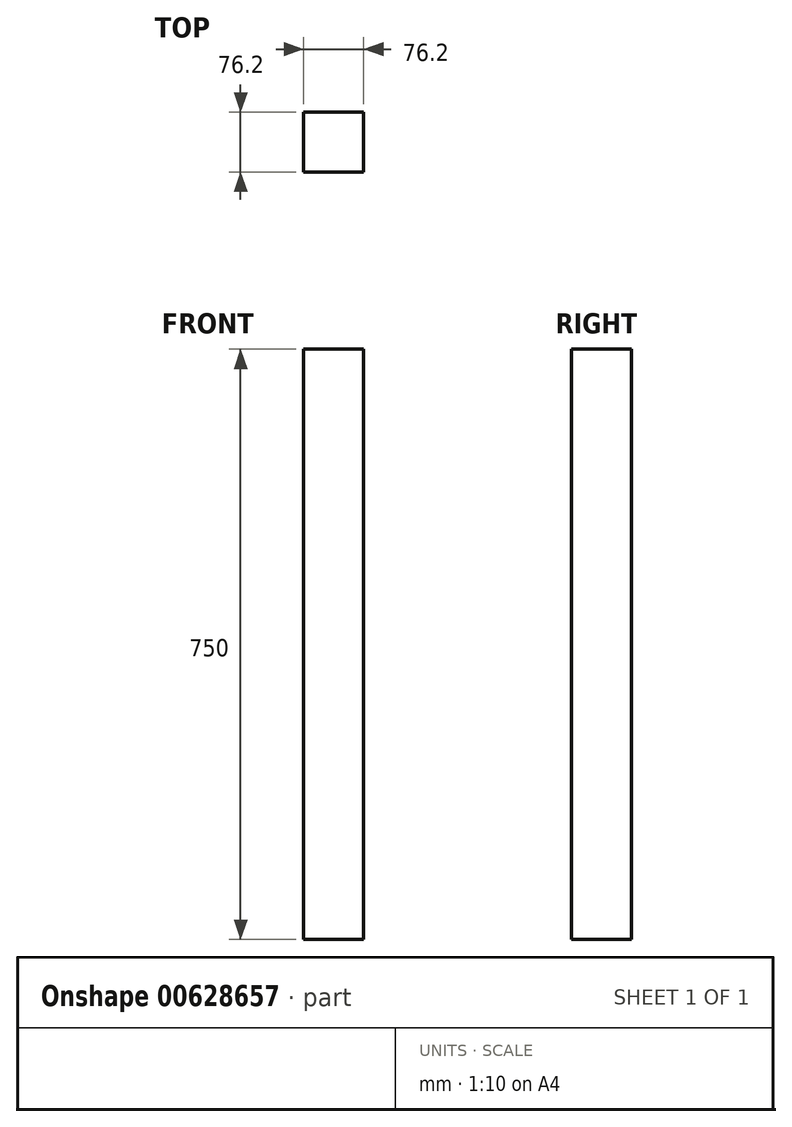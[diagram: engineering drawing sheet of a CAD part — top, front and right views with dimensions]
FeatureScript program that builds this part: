
annotation { "Feature Type Name" : "Feature", "Feature Type Description" : "" }
export const myFeature = defineFeature(function(context is Context, id is Id, definition is map)
    precondition{}
    {
        {
            var Q0;
            Q0=qCreatedBy(makeId("Top.planeOp"),FACE);
            var sketch = newSketch(context, id + "F0", { "sketchPlane" : qUnion([Q0])});
            skLineSegment(sketch, "E0.bottom", {"start": v(-38.1, 38.1) * mm, "end": v(38.1, 38.1) * mm});
            skLineSegment(sketch, "E0.top", {"start": v(-38.1, -38.1) * mm, "end": v(38.1, -38.1) * mm});
            skLineSegment(sketch, "E0.left", {"start": v(-38.1, 38.1) * mm, "end": v(-38.1, -38.1) * mm});
            skLineSegment(sketch, "E0.right", {"start": v(38.1, 38.1) * mm, "end": v(38.1, -38.1) * mm});
            skPoint(sketch, "E0.middle", {"position": v(0, 0) * mm});
            skSolve(sketch);
        }
        {
            var Q0;
            Q0=qSketchRegion(id+"F0",true);
            extrude(context, id + "F1", {"entities" : qUnion([Q0]), "oppositeDirection" : true, "depth" : 750 * mm, "offsetDistance" : 25 * mm});
        }
    });
